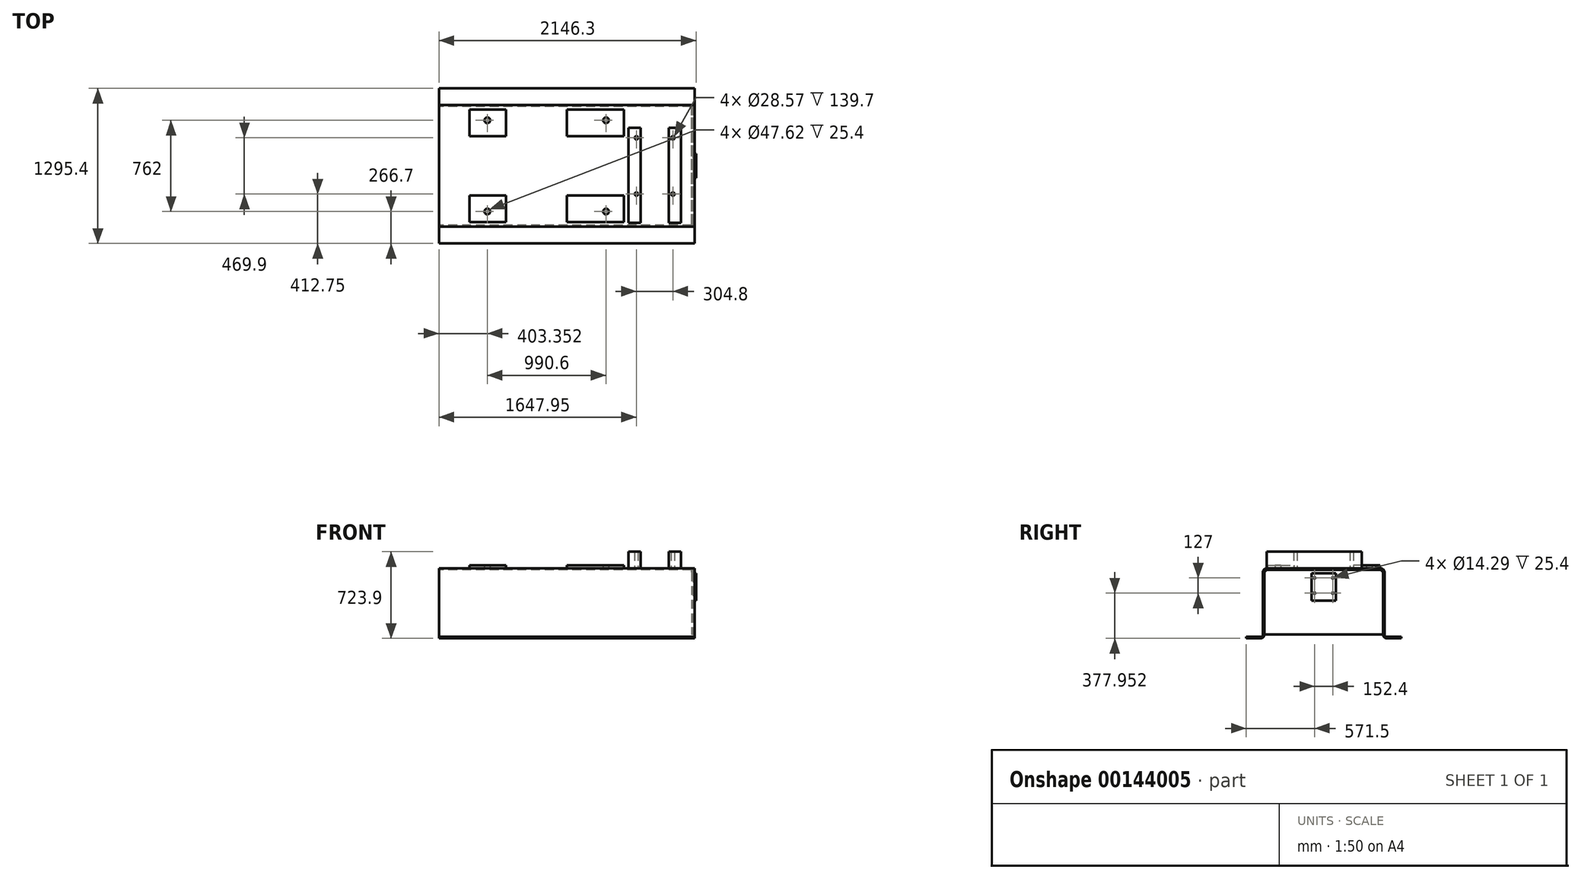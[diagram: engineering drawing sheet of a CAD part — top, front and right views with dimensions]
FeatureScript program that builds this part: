
annotation { "Feature Type Name" : "Feature", "Feature Type Description" : "" }
export const myFeature = defineFeature(function(context is Context, id is Id, definition is map)
    precondition{}
    {
        {
            var Q0;
            Q0=qCreatedBy(makeId("Right.planeOp"),FACE);
            var sketch = newSketch(context, id + "F0", { "sketchPlane" : qUnion([Q0])});
            skLineSegment(sketch, "E0.rect.bottom", {"start": v(-476.25, 292.1) * mm, "end": v(476.25, 292.1) * mm});
            skLineSegment(sketch, "E0.rect.top", {"start": v(-647.7, -292.1) * mm, "end": v(-527.05, -292.1) * mm});
            skLineSegment(sketch, "E0.rect.left", {"start": v(-508, 260.35) * mm, "end": v(-508, -260.35) * mm});
            skLineSegment(sketch, "E0.rect.right", {"start": v(508, 260.35) * mm, "end": v(508, -260.35) * mm});
            skPoint(sketch, "E0.rect.middle", {"position": v(0, 0) * mm});
            skPoint(sketch, "E1.visualSharp", {"position": v(-508, 292.1) * mm});
            skArc(sketch, "E1.filletArc", {"start": v(-476.25, 292.1) * mm, "mid": v(-498.7, 282.8) * mm, "end": v(-508, 260.35) * mm});
            skPoint(sketch, "E2.visualSharp", {"position": v(508, 292.1) * mm});
            skArc(sketch, "E2.filletArc", {"start": v(508, 260.35) * mm, "mid": v(498.7, 282.8) * mm, "end": v(476.25, 292.1) * mm});
            skLineSegment(sketch, "E3.0", {"start": v(-647.7, -279.4) * mm, "end": v(-647.7, -292.1) * mm});
            skLineSegment(sketch, "E4", {"start": v(0, 371.4) * mm, "end": v(0, -436.62) * mm, "construction": true});
            skLineSegment(sketch, "E5.0", {"start": v(-647.7, -279.4) * mm, "end": v(-527.05, -279.4) * mm});
            skPoint(sketch, "E6.newPointA", {"position": v(-508, -292.1) * mm});
            skArc(sketch, "E6.filletArc", {"start": v(-527.05, -279.4) * mm, "mid": v(-513.58, -273.82) * mm, "end": v(-508, -260.35) * mm});
            skLineSegment(sketch, "E7.0", {"start": v(-495.3, 260.35) * mm, "end": v(-495.3, -260.35) * mm});
            skArc(sketch, "E8.0", {"start": v(-527.05, -292.1) * mm, "mid": v(-504.6, -282.8) * mm, "end": v(-495.3, -260.35) * mm});
            skArc(sketch, "E9.0", {"start": v(-476.25, 279.4) * mm, "mid": v(-489.72, 273.82) * mm, "end": v(-495.3, 260.35) * mm});
            skLineSegment(sketch, "E10.0", {"start": v(-476.25, 279.4) * mm, "end": v(476.25, 279.4) * mm});
            skArc(sketch, "E11.0", {"start": v(495.3, 260.35) * mm, "mid": v(489.72, 273.82) * mm, "end": v(476.25, 279.4) * mm});
            skLineSegment(sketch, "E12.0", {"start": v(495.3, 260.35) * mm, "end": v(495.3, -260.35) * mm});
            skArc(sketch, "E13.MirrorCS", {"start": v(527.05, -279.4) * mm, "mid": v(513.58, -273.82) * mm, "end": v(508, -260.35) * mm});
            skLineSegment(sketch, "E14.MirrorCS", {"start": v(647.7, -279.4) * mm, "end": v(647.7, -292.1) * mm});
            skArc(sketch, "E15.MirrorCS", {"start": v(527.05, -292.1) * mm, "mid": v(504.6, -282.8) * mm, "end": v(495.3, -260.35) * mm});
            skLineSegment(sketch, "E16.MirrorCS", {"start": v(647.7, -292.1) * mm, "end": v(527.05, -292.1) * mm});
            skPoint(sketch, "E17.MirrorP", {"position": v(508, -292.1) * mm});
            skLineSegment(sketch, "E18.MirrorCS", {"start": v(647.7, -279.4) * mm, "end": v(527.05, -279.4) * mm});
            skSolve(sketch);
        }
        {
            var Q0;
            Q0=qSketchRegion(id+"F0",true);
            extrude(context, id + "F1", {"entities" : qUnion([Q0]), "endBound" : BoundingType.SYMMETRIC, "depth" : 2133.6 * mm});
        }
        {
            var Q0;
            Q0=makeQuery(id+"F1.opExtrude","SWEPT_FACE",FACE,{"disambiguationData":[OSD([sQuery(id+"F0.wireOp",EDGE,"E0.rect.bottom")])]});
            var sketch = newSketch(context, id + "F2", { "sketchPlane" : qUnion([Q0])});
            skLineSegment(sketch, "E19.0", {"start": v(1066.8, -476.25) * mm, "end": v(1066.8, 476.25) * mm, "construction": true});
            skLineSegment(sketch, "E20.0", {"start": v(733.55, -476.25) * mm, "end": v(733.55, 476.25) * mm, "construction": true});
            skLineSegment(sketch, "E21.0", {"start": v(-168.15, -476.25) * mm, "end": v(-168.15, 476.25) * mm, "construction": true});
            skLineSegment(sketch, "E22", {"start": v(-1066.8, 0) * mm, "end": v(1066.8, 0) * mm, "construction": true});
            skLineSegment(sketch, "E23.0", {"start": v(-1066.8, 317.5) * mm, "end": v(1066.8, 317.5) * mm, "construction": true});
            skLineSegment(sketch, "E24.0", {"start": v(-1066.8, -469.9) * mm, "end": v(1066.8, -469.9) * mm, "construction": true});
            skLineSegment(sketch, "E25.0", {"start": v(850.9, -476.25) * mm, "end": v(850.9, 476.25) * mm, "construction": true});
            skLineSegment(sketch, "E26.0", {"start": v(952.5, -476.25) * mm, "end": v(952.5, 476.25) * mm, "construction": true});
            skLineSegment(sketch, "E27.bottom", {"start": v(952.5, 317.5) * mm, "end": v(850.9, 317.5) * mm});
            skLineSegment(sketch, "E27.top", {"start": v(952.5, -476.25) * mm, "end": v(850.9, -476.25) * mm});
            skLineSegment(sketch, "E27.left", {"start": v(952.5, 317.5) * mm, "end": v(952.5, -476.25) * mm});
            skLineSegment(sketch, "E27.right", {"start": v(850.9, 317.5) * mm, "end": v(850.9, -476.25) * mm});
            skLineSegment(sketch, "E28.0", {"start": v(885.95, -476.25) * mm, "end": v(885.95, 476.25) * mm, "construction": true});
            skLineSegment(sketch, "E29.0", {"start": v(-1066.8, 234.95) * mm, "end": v(1066.8, 234.95) * mm, "construction": true});
            skCircle(sketch, "E30", {"center": v(885.95, 234.95) * mm, "radius": 14.29 * mm});
            skCircle(sketch, "E31.MirrorC", {"center": v(885.95, -234.95) * mm, "radius": 14.29 * mm});
            skCircle(sketch, "E32.MirrorC", {"center": v(581.15, -234.95) * mm, "radius": 14.29 * mm});
            skCircle(sketch, "E33.MirrorC", {"center": v(581.15, 234.95) * mm, "radius": 14.29 * mm});
            skLineSegment(sketch, "E34.MirrorCS", {"start": v(514.6, 317.5) * mm, "end": v(616.2, 317.5) * mm});
            skLineSegment(sketch, "E35.MirrorCS", {"start": v(616.2, 317.5) * mm, "end": v(616.2, -476.25) * mm});
            skLineSegment(sketch, "E36.MirrorCS", {"start": v(514.6, 317.5) * mm, "end": v(514.6, -476.25) * mm});
            skLineSegment(sketch, "E37.MirrorCS", {"start": v(514.6, -476.25) * mm, "end": v(616.2, -476.25) * mm});
            skSolve(sketch);
        }
        {
            var Q0;
            Q0=qSketchRegion(id+"F2",true);
            extrude(context, id + "F3", {"entities" : qUnion([Q0]), "operationType" : NewBodyOperationType.ADD, "depth" : 139.7 * mm});
        }
        {
            var Q0;
            Q0=makeQuery(id+"F2.imprint","IMPRINT",FACE,{"disambiguationData":[TD([[makeQuery(id+"F2.imprint","IMPRINT",EDGE,{"derivedFrom":sQuery(id+"F2.wireOp",EDGE,"E27.bottom")}),-1.0]])]});
            var sketch = newSketch(context, id + "F4", { "sketchPlane" : qUnion([Q0])});
            skLineSegment(sketch, "E38.0", {"start": v(-1066.8, -247.65) * mm, "end": v(1066.8, -247.65) * mm, "construction": true});
            skLineSegment(sketch, "E39.0", {"start": v(-1066.8, -469.9) * mm, "end": v(1066.8, -469.9) * mm, "construction": true});
            skLineSegment(sketch, "E40.0", {"start": v(0, -476.25) * mm, "end": v(0, 476.25) * mm, "construction": true});
            skLineSegment(sketch, "E41.0", {"start": v(476.25, -476.25) * mm, "end": v(476.25, 476.25) * mm, "construction": true});
            skLineSegment(sketch, "E42.0", {"start": v(-508, -476.25) * mm, "end": v(-508, 476.25) * mm, "construction": true});
            skLineSegment(sketch, "E43.0", {"start": v(-812.8, -476.25) * mm, "end": v(-812.8, 476.25) * mm, "construction": true});
            skLineSegment(sketch, "E44.bottom", {"start": v(-508, -469.9) * mm, "end": v(-812.8, -469.9) * mm});
            skLineSegment(sketch, "E44.top", {"start": v(-508, -247.65) * mm, "end": v(-812.8, -247.65) * mm});
            skLineSegment(sketch, "E44.left", {"start": v(-508, -469.9) * mm, "end": v(-508, -247.65) * mm});
            skLineSegment(sketch, "E44.right", {"start": v(-812.8, -469.9) * mm, "end": v(-812.8, -247.65) * mm});
            skLineSegment(sketch, "E45.bottom", {"start": v(476.25, -469.9) * mm, "end": v(0, -469.9) * mm});
            skLineSegment(sketch, "E45.top", {"start": v(476.25, -247.65) * mm, "end": v(0, -247.65) * mm});
            skLineSegment(sketch, "E45.left", {"start": v(476.25, -469.9) * mm, "end": v(476.25, -247.65) * mm});
            skLineSegment(sketch, "E45.right", {"start": v(0, -469.9) * mm, "end": v(0, -247.65) * mm});
            skLineSegment(sketch, "E46.0", {"start": v(-1066.8, -381) * mm, "end": v(1066.8, -381) * mm, "construction": true});
            skLineSegment(sketch, "E47.0", {"start": v(-663.45, -476.25) * mm, "end": v(-663.45, 476.25) * mm, "construction": true});
            skLineSegment(sketch, "E48.0", {"start": v(327.15, -476.25) * mm, "end": v(327.15, 476.25) * mm, "construction": true});
            skCircle(sketch, "E49", {"center": v(-663.45, -381) * mm, "radius": 23.81 * mm});
            skCircle(sketch, "E50", {"center": v(327.15, -381) * mm, "radius": 23.81 * mm});
            skCircle(sketch, "E51.MirrorC", {"center": v(-663.45, 381) * mm, "radius": 23.81 * mm});
            skLineSegment(sketch, "E52.MirrorCS", {"start": v(476.25, 469.9) * mm, "end": v(0, 469.9) * mm});
            skLineSegment(sketch, "E53.MirrorCS", {"start": v(-812.8, 469.9) * mm, "end": v(-812.8, 247.65) * mm});
            skLineSegment(sketch, "E54.MirrorCS", {"start": v(476.25, 469.9) * mm, "end": v(476.25, 247.65) * mm});
            skLineSegment(sketch, "E55.MirrorCS", {"start": v(-508, 469.9) * mm, "end": v(-508, 247.65) * mm});
            skLineSegment(sketch, "E56.MirrorCS", {"start": v(-508, 469.9) * mm, "end": v(-812.8, 469.9) * mm});
            skCircle(sketch, "E57.MirrorC", {"center": v(327.15, 381) * mm, "radius": 23.81 * mm});
            skLineSegment(sketch, "E58.MirrorCS", {"start": v(476.25, 247.65) * mm, "end": v(0, 247.65) * mm});
            skLineSegment(sketch, "E59.MirrorCS", {"start": v(-508, 247.65) * mm, "end": v(-812.8, 247.65) * mm});
            skLineSegment(sketch, "E60.MirrorCS", {"start": v(0, 469.9) * mm, "end": v(0, 247.65) * mm});
            skSolve(sketch);
        }
        {
            var Q0;
            Q0=qSketchRegion(id+"F4",true);
            extrude(context, id + "F5", {"entities" : qUnion([Q0]), "operationType" : NewBodyOperationType.ADD, "depth" : 25.4 * mm});
        }
        {
            var Q0;
            Q0=makeQuery(id+"F1.opExtrude","CAP_FACE",FACE,{"disambiguationData":[OSD([sQuery(id+"F0.wireOp",EDGE,"E0.rect.bottom"),sQuery(id+"F0.wireOp",EDGE,"E0.rect.top"),sQuery(id+"F0.wireOp",EDGE,"E0.rect.left"),sQuery(id+"F0.wireOp",EDGE,"E0.rect.right"),sQuery(id+"F0.wireOp",EDGE,"E1.filletArc"),sQuery(id+"F0.wireOp",EDGE,"E2.filletArc"),sQuery(id+"F0.wireOp",EDGE,"E3.0"),sQuery(id+"F0.wireOp",EDGE,"E5.0"),sQuery(id+"F0.wireOp",EDGE,"E6.filletArc"),sQuery(id+"F0.wireOp",EDGE,"E7.0"),sQuery(id+"F0.wireOp",EDGE,"E8.0"),sQuery(id+"F0.wireOp",EDGE,"E9.0"),sQuery(id+"F0.wireOp",EDGE,"E10.0"),sQuery(id+"F0.wireOp",EDGE,"E12.0"),sQuery(id+"F0.wireOp",EDGE,"E11.0"),sQuery(id+"F0.wireOp",EDGE,"E13.MirrorCS"),sQuery(id+"F0.wireOp",EDGE,"E14.MirrorCS"),sQuery(id+"F0.wireOp",EDGE,"E15.MirrorCS"),sQuery(id+"F0.wireOp",EDGE,"E16.MirrorCS"),sQuery(id+"F0.wireOp",EDGE,"E18.MirrorCS")])],"isStart":false});
            cPlane(context, id + "F6", {"entities" : qUnion([Q0]), "cplaneType" : CPlaneType.OFFSET, "offset" : 25.4 * mm, "oppositeDirection" : true, "width" : 152.4 * mm, "height" : 152.4 * mm});
        }
        {
            var Q0;
            Q0=qCreatedBy(id+"F6.planeOp",FACE);
            var sketch = newSketch(context, id + "F7", { "sketchPlane" : qUnion([Q0])});
            skLineSegment(sketch, "E61.0", {"start": v(495.3, 260.35) * mm, "end": v(495.3, -260.35) * mm});
            skLineSegment(sketch, "E62.0", {"start": v(-476.25, 279.4) * mm, "end": v(476.25, 279.4) * mm});
            skLineSegment(sketch, "E63.0", {"start": v(-495.3, 260.35) * mm, "end": v(-495.3, -260.35) * mm});
            skLineSegment(sketch, "E64", {"start": v(-495.3, 260.35) * mm, "end": v(-476.25, 279.4) * mm});
            skLineSegment(sketch, "E65", {"start": v(476.25, 279.4) * mm, "end": v(495.3, 260.35) * mm});
            skLineSegment(sketch, "E66", {"start": v(-495.3, -260.35) * mm, "end": v(495.3, -260.35) * mm});
            skSolve(sketch);
        }
        {
            var Q0;
            Q0=qSketchRegion(id+"F7",true);
            extrude(context, id + "F8", {"entities" : qUnion([Q0]), "operationType" : NewBodyOperationType.ADD, "depth" : 12.7 * mm});
        }
        {
            var Q0;
            Q0=makeQuery(id+"F8.opExtrude","CAP_FACE",FACE,{"disambiguationData":[OSD([sQuery(id+"F7.wireOp",EDGE,"E61.0"),sQuery(id+"F7.wireOp",EDGE,"E62.0"),sQuery(id+"F7.wireOp",EDGE,"E63.0"),sQuery(id+"F7.wireOp",EDGE,"E64"),sQuery(id+"F7.wireOp",EDGE,"E65"),sQuery(id+"F7.wireOp",EDGE,"E66")])],"isStart":false});
            var sketch = newSketch(context, id + "F9", { "sketchPlane" : qUnion([Q0])});
            skLineSegment(sketch, "E67.0", {"start": v(317.5, 431.8) * mm, "end": v(-476.25, 431.8) * mm, "construction": true});
            skLineSegment(sketch, "E68.0", {"start": v(317.5, 212.85) * mm, "end": v(-476.25, 212.85) * mm, "construction": true});
            skLineSegment(sketch, "E69.0", {"start": v(317.5, 85.85) * mm, "end": v(-476.25, 85.85) * mm, "construction": true});
            skLineSegment(sketch, "E70.0", {"start": v(647.7, 250.83) * mm, "end": v(0, 250.83) * mm, "construction": true});
            skLineSegment(sketch, "E71", {"start": v(0, 0) * mm, "end": v(0, 378.53) * mm, "construction": true});
            skLineSegment(sketch, "E72.0", {"start": v(647.7, 22.23) * mm, "end": v(0, 22.23) * mm, "construction": true});
            skLineSegment(sketch, "E73.0", {"start": v(101.6, 0) * mm, "end": v(101.6, 378.53) * mm, "construction": true});
            skLineSegment(sketch, "E74.0", {"start": v(76.2, 0) * mm, "end": v(76.2, 378.53) * mm, "construction": true});
            skLineSegment(sketch, "E75.bottom", {"start": v(101.6, 250.83) * mm, "end": v(0, 250.83) * mm});
            skLineSegment(sketch, "E75.top", {"start": v(101.6, 22.23) * mm, "end": v(0, 22.23) * mm});
            skLineSegment(sketch, "E75.left", {"start": v(101.6, 250.83) * mm, "end": v(101.6, 22.23) * mm});
            skLineSegment(sketch, "E75.right", {"start": v(0, 250.83) * mm, "end": v(0, 22.23) * mm});
            skCircle(sketch, "E76", {"center": v(76.2, 212.85) * mm, "radius": 7.14 * mm});
            skCircle(sketch, "E77", {"center": v(76.2, 85.85) * mm, "radius": 7.14 * mm});
            skCircle(sketch, "E78.MirrorC", {"center": v(-76.2, 85.85) * mm, "radius": 7.14 * mm});
            skCircle(sketch, "E79.MirrorC", {"center": v(-76.2, 212.85) * mm, "radius": 7.14 * mm});
            skLineSegment(sketch, "E80.MirrorCS", {"start": v(-101.6, 250.83) * mm, "end": v(0, 250.83) * mm});
            skLineSegment(sketch, "E81.MirrorCS", {"start": v(-101.6, 22.23) * mm, "end": v(0, 22.23) * mm});
            skLineSegment(sketch, "E82.MirrorCS", {"start": v(-101.6, 250.83) * mm, "end": v(-101.6, 22.23) * mm});
            skSolve(sketch);
        }
        {
            var Q0;
            Q0=qSketchRegion(id+"F9",true);
            extrude(context, id + "F10", {"entities" : qUnion([Q0]), "operationType" : NewBodyOperationType.ADD, "depth" : 25.4 * mm});
        }
    });
